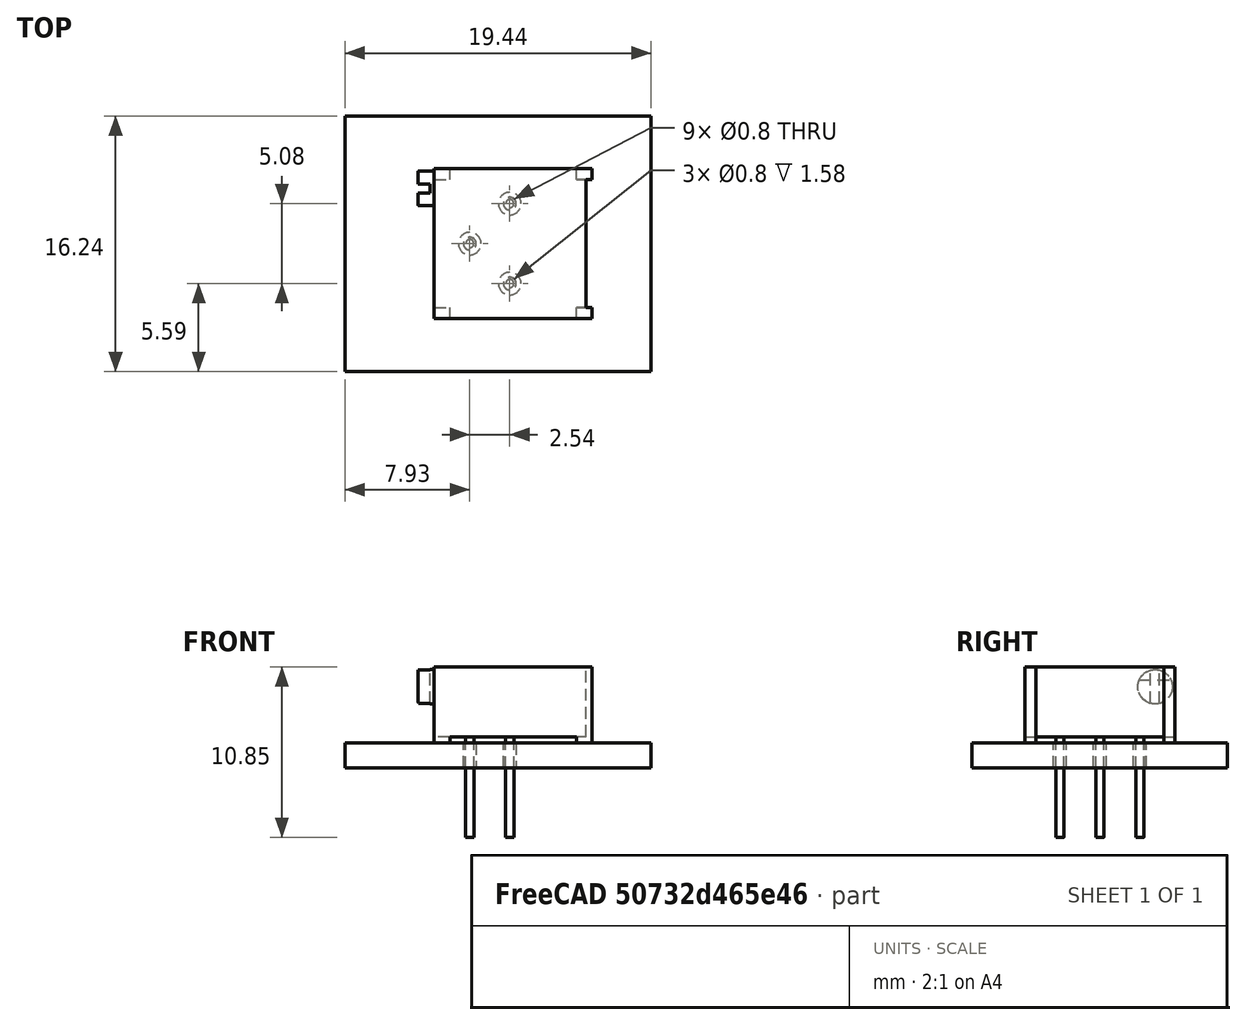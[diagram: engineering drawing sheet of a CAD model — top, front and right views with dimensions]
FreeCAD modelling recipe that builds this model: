
FCSTD DOCUMENT  (FreeCAD 0.18R15611 (Git))
Label: Potentiometer_Bourns_3296P_Horizontal
License: All rights reserved
LicenseURL: http://en.wikipedia.org/wiki/All_rights_reserved
objects: Part::FeaturePython×7, Part::Box×6, Part::Cylinder×4, Part::MultiFuse×2, App::DocumentObjectGroup×1, Part::Cut×1, Part::Feature×1
note: 21 computed .brp shape members not serialized (recipe doc carries the construction recipe); baked Part::Feature solids carry a one-line shape summary decoded from their .brp

FEATURE [Part::FeaturePython] FCrtYd_lines  label="FCrtYd"  # a2plus imported part (geometry in sourceFile) (typed FeaturePython)
  fixedPosition = true
FEATURE [Part::FeaturePython] FFab_lines  label="FFab"  # a2plus imported part (geometry in sourceFile) (typed FeaturePython)
  fixedPosition = true
FEATURE [Part::FeaturePython] Filk_lines  label="FrontSilk"  # a2plus imported part (geometry in sourceFile) (typed FeaturePython)
  fixedPosition = true
FEATURE [Part::FeaturePython] TopPads  # a2plus imported part (geometry in sourceFile) (typed FeaturePython)
  fixedPosition = true
FEATURE [Part::FeaturePython] BotPads  # a2plus imported part (geometry in sourceFile) (typed FeaturePython)
  fixedPosition = true
FEATURE [Part::FeaturePython] THPs  label="PTHs"  # a2plus imported part (geometry in sourceFile) (typed FeaturePython)
  fixedPosition = true
FEATURE [Part::FeaturePython] newPCB  label="Pcb"  # a2plus imported part (geometry in sourceFile) (typed FeaturePython)
  fixedPosition = true
FEATURE [App::DocumentObjectGroup] Potentiometer_Bourns_3296P_Horizontal_fp
  Group = -> [FCrtYd_lines,FFab_lines,Filk_lines,TopPads,BotPads,THPs,newPCB]
FEATURE [Part::Cylinder] Cylinder001  label="Pin3"
  Angle = 360
  AttacherType = Attacher::AttachEngine3D
  Height = 6.4
  Placement = pos=(0,-5.08,-6.02) rot=(0,0,1;0rad)
  Radius = 0.255
FEATURE [Part::Cylinder] Cylinder  label="Pin1"
  Angle = 360
  AttacherType = Attacher::AttachEngine3D
  Height = 6.4
  Placement = pos=(0,0,-6.02) rot=(0,0,1;0rad)
  Radius = 0.255
FEATURE [Part::Cylinder] Cylinder002  label="Pin2"
  Angle = 360
  AttacherType = Attacher::AttachEngine3D
  Height = 6.4
  Placement = pos=(-2.54,-2.54,-6.02) rot=(0,0,1;0rad)
  Radius = 0.255
FEATURE [Part::Cylinder] Cylinder003  label="Knob"
  Angle = 360
  AttacherType = Attacher::AttachEngine3D
  Height = 1.02
  Placement = pos=(-0.405,-2.25,7.24) rot=(0,0,1;0rad)
  Radius = 1.095
FEATURE [Part::Box] Box003  label="Cube001"
  AttacherType = Attacher::AttachEngine3D
  Height = 0.76
  Length = 10
  Placement = pos=(-5,-2.54,7.5) rot=(0,0,1;0rad)
  Width = 0.56
FEATURE [Part::Cut] Cut  label="CutKnob"
  Base = -> Cylinder003
  Placement = pos=(2.44,3.22,4.03) rot=(0,-1,0;1.57931rad)
  Refine = true
  Tool = -> Box003
FEATURE [Part::Box] Box  label="Body"
  AttacherType = Attacher::AttachEngine3D
  Height = 4.45
  Length = 9.65
  Placement = pos=(0,0,0.38) rot=(0,0,1;0rad)
  Width = 9.53
FEATURE [Part::Box] Box004  label="StandoffFront"
  AttacherType = Attacher::AttachEngine3D
  Height = 4.83
  Length = 1
  Width = 0.7
FEATURE [Part::Box] Box005  label="StandoffBack"
  AttacherType = Attacher::AttachEngine3D
  Height = 4.83
  Length = 1
  Placement = pos=(9.03,0,0) rot=(0,0,1;0rad)
  Width = 0.7
FEATURE [Part::Box] Box006  label="StandoffFront001"
  AttacherType = Attacher::AttachEngine3D
  Height = 4.83
  Length = 1
  Placement = pos=(0,8.83,0) rot=(0,0,1;0rad)
  Width = 0.7
FEATURE [Part::Box] Box007  label="StandoffBack001"
  AttacherType = Attacher::AttachEngine3D
  Height = 4.83
  Length = 1
  Placement = pos=(9.03,8.83,0) rot=(0,0,1;0rad)
  Width = 0.7
FEATURE [Part::MultiFuse] Fusion  label="FusionBody"
  Placement = pos=(-4.8,-7.3,0) rot=(0,0,1;0rad)
  Refine = true
  Shapes = -> [Box,Box004,Box005,Box006,Box007]
FEATURE [Part::MultiFuse] Pin2_mp_cp  label="Pin2_fd"
  Refine = true
  Shapes = -> [Cylinder002,Cylinder,Cylinder001,Cut,Fusion]
FEATURE [Part::Feature] Shape  label="Potentiometer_Bourns_3296P_Horizontal"
  shape: bbox 11.06 x 9.53 x 10.85 mm, 33 faces (baked)
